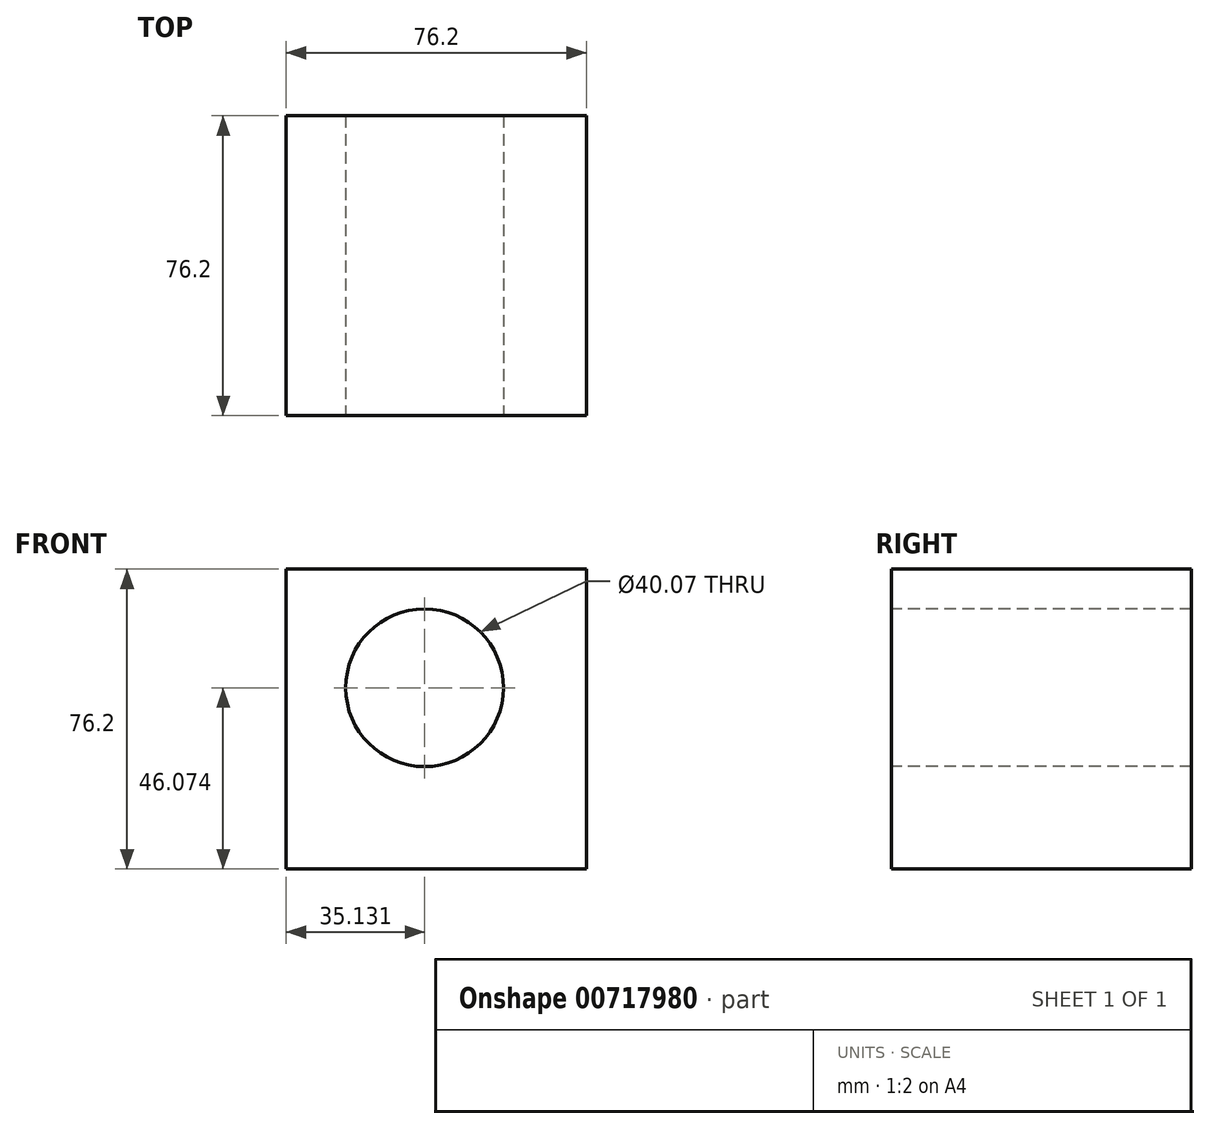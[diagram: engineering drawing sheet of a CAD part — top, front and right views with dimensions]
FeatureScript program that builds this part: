
annotation { "Feature Type Name" : "Feature", "Feature Type Description" : "" }
export const myFeature = defineFeature(function(context is Context, id is Id, definition is map)
    precondition{}
    {
        {
            var Q0;
            Q0=qCreatedBy(makeId("Front.planeOp"),FACE);
            var sketch = newSketch(context, id + "F0", { "sketchPlane" : qUnion([Q0])});
            skLineSegment(sketch, "E0.bottom", {"start": v(-37.5, 38.64) * mm, "end": v(38.7, 38.64) * mm});
            skLineSegment(sketch, "E0.top", {"start": v(-37.5, -37.56) * mm, "end": v(38.7, -37.56) * mm});
            skLineSegment(sketch, "E0.left", {"start": v(-37.5, 38.64) * mm, "end": v(-37.5, -37.56) * mm});
            skLineSegment(sketch, "E0.right", {"start": v(38.7, 38.64) * mm, "end": v(38.7, -37.56) * mm});
            skSolve(sketch);
        }
        {
            var Q0;
            Q0=makeQuery(id+"F0.imprint","IMPRINT",FACE,{"disambiguationData":[TD([[makeQuery(id+"F0.imprint","IMPRINT",EDGE,{"derivedFrom":sQuery(id+"F0.wireOp",EDGE,"E0.bottom")}),-1.0]])]});
            extrude(context, id + "F1", {"entities" : qUnion([Q0]), "depth" : 76.2 * mm, "offsetDistance" : 25.4 * mm});
        }
        {
            var Q0;
            Q0=makeQuery(id+"F1.opExtrude","CAP_FACE",FACE,{"disambiguationData":[OSD([sQuery(id+"F0.wireOp",EDGE,"E0.bottom"),sQuery(id+"F0.wireOp",EDGE,"E0.top"),sQuery(id+"F0.wireOp",EDGE,"E0.left"),sQuery(id+"F0.wireOp",EDGE,"E0.right")])],"isStart":false});
            var sketch = newSketch(context, id + "F2", { "sketchPlane" : qUnion([Q0])});
            skCircle(sketch, "E1", {"center": v(-2.38, 8.51) * mm, "radius": 20.04 * mm});
            skSolve(sketch);
        }
        {
            var Q0;
            Q0=makeQuery(id+"F2.imprint","IMPRINT",FACE,{"disambiguationData":[TD([[makeQuery(id+"F2.imprint","IMPRINT",EDGE,{"derivedFrom":sQuery(id+"F2.wireOp",EDGE,"E1")}),1.0]])]});
            extrude(context, id + "F3", {"entities" : qUnion([Q0]), "operationType" : NewBodyOperationType.ADD, "endBound" : BoundingType.THROUGH_ALL, "oppositeDirection" : true, "depth" : 50.8 * mm, "offsetDistance" : 25.4 * mm});
        }
        {
            var Q0;
            Q0=makeQuery(id+"F3.opExtrude","CAP_FACE",FACE,{"disambiguationData":[OSD([sQuery(id+"F2.wireOp",EDGE,"E1")])],"isStart":false});
            extrude(context, id + "F4", {"entities" : qUnion([Q0]), "endBound" : BoundingType.THROUGH_ALL, "oppositeDirection" : true, "depth" : 25.4 * mm, "offsetDistance" : 25.4 * mm});
        }
        {
            var Q0;
            Q0=makeQuery(id+"F4.opExtrude","CAP_FACE",FACE,{"disambiguationData":[OSD([sQuery(id+"F2.wireOp",EDGE,"E1")])],"isStart":false});
            extrude(context, id + "F5", {"entities" : qUnion([Q0]), "operationType" : NewBodyOperationType.REMOVE, "endBound" : BoundingType.THROUGH_ALL, "oppositeDirection" : true, "depth" : 60.96 * mm, "offsetDistance" : 25.4 * mm});
        }
    });
